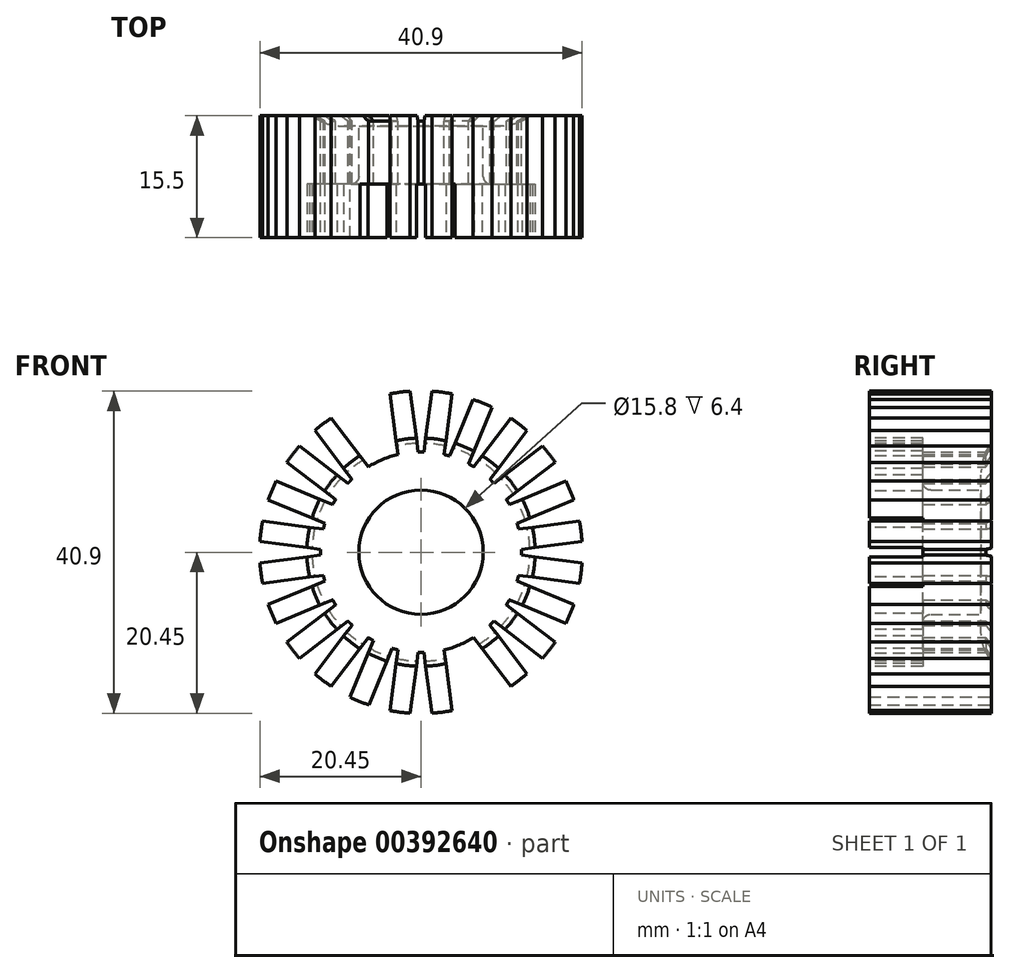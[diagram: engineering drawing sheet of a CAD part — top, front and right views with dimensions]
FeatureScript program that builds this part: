
annotation { "Feature Type Name" : "Feature", "Feature Type Description" : "" }
export const myFeature = defineFeature(function(context is Context, id is Id, definition is map)
    precondition{}
    {
        {
            var Q0;
            Q0=qCreatedBy(makeId("Front.planeOp"),FACE);
            var sketch = newSketch(context, id + "F0", { "sketchPlane" : qUnion([Q0])});
            skCircle(sketch, "E0", {"center": v(0, 0) * mm, "radius": 7.9 * mm});
            skCircle(sketch, "E1", {"center": v(0, 0) * mm, "radius": 12.75 * mm});
            skLineSegment(sketch, "E2", {"start": v(-29.1, 0) * mm, "end": v(30.08, 0) * mm, "construction": true});
            skLineSegment(sketch, "E3", {"start": v(4.61, 35.03) * mm, "end": v(-4.61, -35.03) * mm, "construction": true});
            skLineSegment(sketch, "E4", {"start": v(0.37, 12.74) * mm, "end": v(1.38, 20.45) * mm});
            skLineSegment(sketch, "E5", {"start": v(2.94, 12.4) * mm, "end": v(3.96, 20.11) * mm});
            skArc(sketch, "E6.trimOffspring", {"start": v(3.96, 20.11) * mm, "mid": v(2.68, 20.32) * mm, "end": v(1.38, 20.45) * mm});
            skLineSegment(sketch, "E7.1.0", {"start": v(6.05, 11.22) * mm, "end": v(9.03, 18.4) * mm});
            skArc(sketch, "E7.1.1", {"start": v(9.03, 18.4) * mm, "mid": v(7.85, 18.94) * mm, "end": v(6.63, 19.4) * mm});
            skLineSegment(sketch, "E7.1.2", {"start": v(3.65, 12.22) * mm, "end": v(6.63, 19.4) * mm});
            skLineSegment(sketch, "E7.2.0", {"start": v(8.75, 9.27) * mm, "end": v(13.49, 15.44) * mm});
            skArc(sketch, "E7.2.1", {"start": v(13.49, 15.44) * mm, "mid": v(12.48, 16.26) * mm, "end": v(11.42, 17.02) * mm});
            skLineSegment(sketch, "E7.2.2", {"start": v(6.69, 10.85) * mm, "end": v(11.42, 17.02) * mm});
            skLineSegment(sketch, "E7.3.0", {"start": v(10.85, 6.69) * mm, "end": v(17.02, 11.42) * mm});
            skArc(sketch, "E7.3.1", {"start": v(17.02, 11.42) * mm, "mid": v(16.26, 12.48) * mm, "end": v(15.44, 13.49) * mm});
            skLineSegment(sketch, "E7.3.2", {"start": v(9.27, 8.75) * mm, "end": v(15.44, 13.49) * mm});
            skLineSegment(sketch, "E7.4.0", {"start": v(12.22, 3.65) * mm, "end": v(19.4, 6.63) * mm});
            skArc(sketch, "E7.4.1", {"start": v(19.4, 6.63) * mm, "mid": v(18.94, 7.85) * mm, "end": v(18.4, 9.03) * mm});
            skLineSegment(sketch, "E7.4.2", {"start": v(11.22, 6.05) * mm, "end": v(18.4, 9.03) * mm});
            skLineSegment(sketch, "E7.5.0", {"start": v(12.74, 0.37) * mm, "end": v(20.45, 1.38) * mm});
            skArc(sketch, "E7.5.1", {"start": v(20.45, 1.38) * mm, "mid": v(20.32, 2.68) * mm, "end": v(20.11, 3.96) * mm});
            skLineSegment(sketch, "E7.5.2", {"start": v(12.4, 2.94) * mm, "end": v(20.11, 3.96) * mm});
            skLineSegment(sketch, "E7.6.0", {"start": v(12.4, -2.94) * mm, "end": v(20.11, -3.96) * mm});
            skArc(sketch, "E7.6.1", {"start": v(20.11, -3.96) * mm, "mid": v(20.32, -2.68) * mm, "end": v(20.45, -1.38) * mm});
            skLineSegment(sketch, "E7.6.2", {"start": v(12.74, -0.37) * mm, "end": v(20.45, -1.38) * mm});
            skLineSegment(sketch, "E7.7.0", {"start": v(11.22, -6.05) * mm, "end": v(18.4, -9.03) * mm});
            skArc(sketch, "E7.7.1", {"start": v(18.4, -9.03) * mm, "mid": v(18.94, -7.85) * mm, "end": v(19.4, -6.63) * mm});
            skLineSegment(sketch, "E7.7.2", {"start": v(12.22, -3.65) * mm, "end": v(19.4, -6.63) * mm});
            skLineSegment(sketch, "E7.anchor1", {"start": v(0, 0) * mm, "end": v(2.94, 12.4) * mm, "construction": true});
            skLineSegment(sketch, "E7.anchor2", {"start": v(0, 0) * mm, "end": v(-0.37, 12.74) * mm, "construction": true});
            skLineSegment(sketch, "E8.1.8.0", {"start": v(9.27, -8.75) * mm, "end": v(15.44, -13.49) * mm});
            skArc(sketch, "E8.3.8.0", {"start": v(15.44, -13.49) * mm, "mid": v(16.26, -12.48) * mm, "end": v(17.02, -11.42) * mm});
            skLineSegment(sketch, "E8.7.8.0", {"start": v(10.85, -6.69) * mm, "end": v(17.02, -11.42) * mm});
            skLineSegment(sketch, "E8.1.9.0", {"start": v(6.69, -10.85) * mm, "end": v(11.42, -17.02) * mm});
            skArc(sketch, "E8.3.9.0", {"start": v(11.42, -17.02) * mm, "mid": v(12.48, -16.26) * mm, "end": v(13.49, -15.44) * mm});
            skLineSegment(sketch, "E8.7.9.0", {"start": v(8.75, -9.27) * mm, "end": v(13.49, -15.44) * mm});
            skLineSegment(sketch, "E8.1.10.0", {"start": v(3.65, -12.22) * mm, "end": v(6.63, -19.4) * mm});
            skArc(sketch, "E8.3.10.0", {"start": v(6.63, -19.4) * mm, "mid": v(7.85, -18.94) * mm, "end": v(9.03, -18.4) * mm});
            skLineSegment(sketch, "E8.7.10.0", {"start": v(6.05, -11.22) * mm, "end": v(9.03, -18.4) * mm});
            skLineSegment(sketch, "E8.1.11.0", {"start": v(0.37, -12.74) * mm, "end": v(1.38, -20.45) * mm});
            skArc(sketch, "E8.3.11.0", {"start": v(1.38, -20.45) * mm, "mid": v(2.68, -20.32) * mm, "end": v(3.96, -20.11) * mm});
            skLineSegment(sketch, "E8.7.11.0", {"start": v(2.94, -12.4) * mm, "end": v(3.96, -20.11) * mm});
            skLineSegment(sketch, "E8.1.12.0", {"start": v(-2.94, -12.4) * mm, "end": v(-3.96, -20.11) * mm});
            skArc(sketch, "E8.3.12.0", {"start": v(-3.96, -20.11) * mm, "mid": v(-2.68, -20.32) * mm, "end": v(-1.38, -20.45) * mm});
            skLineSegment(sketch, "E8.7.12.0", {"start": v(-0.37, -12.74) * mm, "end": v(-1.38, -20.45) * mm});
            skLineSegment(sketch, "E8.1.13.0", {"start": v(-6.05, -11.22) * mm, "end": v(-9.03, -18.4) * mm});
            skArc(sketch, "E8.3.13.0", {"start": v(-9.03, -18.4) * mm, "mid": v(-7.85, -18.94) * mm, "end": v(-6.63, -19.4) * mm});
            skLineSegment(sketch, "E8.7.13.0", {"start": v(-3.65, -12.22) * mm, "end": v(-6.63, -19.4) * mm});
            skLineSegment(sketch, "E8.1.14.0", {"start": v(-8.75, -9.27) * mm, "end": v(-13.49, -15.44) * mm});
            skArc(sketch, "E8.3.14.0", {"start": v(-13.49, -15.44) * mm, "mid": v(-12.48, -16.26) * mm, "end": v(-11.42, -17.02) * mm});
            skLineSegment(sketch, "E8.7.14.0", {"start": v(-6.69, -10.85) * mm, "end": v(-11.42, -17.02) * mm});
            skLineSegment(sketch, "E8.1.15.0", {"start": v(-10.85, -6.69) * mm, "end": v(-17.02, -11.42) * mm});
            skArc(sketch, "E8.3.15.0", {"start": v(-17.02, -11.42) * mm, "mid": v(-16.26, -12.48) * mm, "end": v(-15.44, -13.49) * mm});
            skLineSegment(sketch, "E8.7.15.0", {"start": v(-9.27, -8.75) * mm, "end": v(-15.44, -13.49) * mm});
            skLineSegment(sketch, "E8.1.16.0", {"start": v(-12.22, -3.65) * mm, "end": v(-19.4, -6.63) * mm});
            skArc(sketch, "E8.3.16.0", {"start": v(-19.4, -6.63) * mm, "mid": v(-18.94, -7.85) * mm, "end": v(-18.4, -9.03) * mm});
            skLineSegment(sketch, "E8.7.16.0", {"start": v(-11.22, -6.05) * mm, "end": v(-18.4, -9.03) * mm});
            skLineSegment(sketch, "E8.1.17.0", {"start": v(-12.74, -0.37) * mm, "end": v(-20.45, -1.38) * mm});
            skArc(sketch, "E8.3.17.0", {"start": v(-20.45, -1.38) * mm, "mid": v(-20.32, -2.68) * mm, "end": v(-20.11, -3.96) * mm});
            skLineSegment(sketch, "E8.7.17.0", {"start": v(-12.4, -2.94) * mm, "end": v(-20.11, -3.96) * mm});
            skLineSegment(sketch, "E8.1.18.0", {"start": v(-12.4, 2.94) * mm, "end": v(-20.11, 3.96) * mm});
            skArc(sketch, "E8.3.18.0", {"start": v(-20.11, 3.96) * mm, "mid": v(-20.32, 2.68) * mm, "end": v(-20.45, 1.38) * mm});
            skLineSegment(sketch, "E8.7.18.0", {"start": v(-12.74, 0.37) * mm, "end": v(-20.45, 1.38) * mm});
            skLineSegment(sketch, "E8.1.19.0", {"start": v(-11.22, 6.05) * mm, "end": v(-18.4, 9.03) * mm});
            skArc(sketch, "E8.3.19.0", {"start": v(-18.4, 9.03) * mm, "mid": v(-18.94, 7.85) * mm, "end": v(-19.4, 6.63) * mm});
            skLineSegment(sketch, "E8.7.19.0", {"start": v(-12.22, 3.65) * mm, "end": v(-19.4, 6.63) * mm});
            skLineSegment(sketch, "E8.1.20.0", {"start": v(-9.27, 8.75) * mm, "end": v(-15.44, 13.49) * mm});
            skArc(sketch, "E8.3.20.0", {"start": v(-15.44, 13.49) * mm, "mid": v(-16.26, 12.48) * mm, "end": v(-17.02, 11.42) * mm});
            skLineSegment(sketch, "E8.7.20.0", {"start": v(-10.85, 6.69) * mm, "end": v(-17.02, 11.42) * mm});
            skLineSegment(sketch, "E8.1.21.0", {"start": v(-6.69, 10.85) * mm, "end": v(-11.42, 17.02) * mm});
            skArc(sketch, "E8.3.21.0", {"start": v(-11.42, 17.02) * mm, "mid": v(-12.48, 16.26) * mm, "end": v(-13.49, 15.44) * mm});
            skLineSegment(sketch, "E8.7.21.0", {"start": v(-8.75, 9.27) * mm, "end": v(-13.49, 15.44) * mm});
            skLineSegment(sketch, "E8.1.22.0", {"start": v(-3.65, 12.22) * mm, "end": v(-6.63, 19.4) * mm});
            skArc(sketch, "E8.3.22.0", {"start": v(-6.63, 19.4) * mm, "mid": v(-7.85, 18.94) * mm, "end": v(-9.03, 18.4) * mm});
            skLineSegment(sketch, "E8.7.22.0", {"start": v(-6.05, 11.22) * mm, "end": v(-9.03, 18.4) * mm});
            skLineSegment(sketch, "E8.1.23.0", {"start": v(-0.37, 12.74) * mm, "end": v(-1.38, 20.45) * mm});
            skArc(sketch, "E8.3.23.0", {"start": v(-1.38, 20.45) * mm, "mid": v(-2.68, 20.32) * mm, "end": v(-3.96, 20.11) * mm});
            skLineSegment(sketch, "E8.7.23.0", {"start": v(-2.94, 12.4) * mm, "end": v(-3.96, 20.11) * mm});
            skPoint(sketch, "E9", {"position": v(-16.26, 12.48) * mm});
            skPoint(sketch, "E10", {"position": v(16.26, -12.48) * mm});
            skSolve(sketch);
        }
        {
            var Q0;
            Q0=qSketchRegion(id+"F0",true);
            extrude(context, id + "F1", {"entities" : qUnion([Q0]), "depth" : 15.5 * mm});
        }
        {
            var Q0;
            Q0=makeQuery(id+"F1.opExtrude","CAP_FACE",FACE,{"disambiguationData":[OSD([sQuery(id+"F0.wireOp",EDGE,"E0"),sQuery(id+"F0.wireOp",EDGE,"E1"),sQuery(id+"F0.wireOp",EDGE,"E4"),sQuery(id+"F0.wireOp",EDGE,"E5"),sQuery(id+"F0.wireOp",EDGE,"E6.trimOffspring"),sQuery(id+"F0.wireOp",EDGE,"E7.1.0"),sQuery(id+"F0.wireOp",EDGE,"E7.1.1"),sQuery(id+"F0.wireOp",EDGE,"E7.1.2"),sQuery(id+"F0.wireOp",EDGE,"E7.2.0"),sQuery(id+"F0.wireOp",EDGE,"E7.2.1"),sQuery(id+"F0.wireOp",EDGE,"E7.2.2"),sQuery(id+"F0.wireOp",EDGE,"E7.3.0"),sQuery(id+"F0.wireOp",EDGE,"E7.3.1"),sQuery(id+"F0.wireOp",EDGE,"E7.3.2"),sQuery(id+"F0.wireOp",EDGE,"E7.4.0"),sQuery(id+"F0.wireOp",EDGE,"E7.4.1"),sQuery(id+"F0.wireOp",EDGE,"E7.4.2"),sQuery(id+"F0.wireOp",EDGE,"E7.5.0"),sQuery(id+"F0.wireOp",EDGE,"E7.5.1"),sQuery(id+"F0.wireOp",EDGE,"E7.5.2"),sQuery(id+"F0.wireOp",EDGE,"E7.6.0"),sQuery(id+"F0.wireOp",EDGE,"E7.6.1"),sQuery(id+"F0.wireOp",EDGE,"E7.6.2"),sQuery(id+"F0.wireOp",EDGE,"E7.7.0"),sQuery(id+"F0.wireOp",EDGE,"E7.7.1"),sQuery(id+"F0.wireOp",EDGE,"E7.7.2")])],"isStart":false});
            var sketch = newSketch(context, id + "F2", { "sketchPlane" : qUnion([Q0])});
            skCircle(sketch, "E11", {"center": v(0, 0) * mm, "radius": 12.75 * mm});
            skSolve(sketch);
        }
        {
            var Q0;
            Q0=qSketchRegion(id+"F2",true);
            extrude(context, id + "F3", {"entities" : qUnion([Q0]), "operationType" : NewBodyOperationType.REMOVE, "oppositeDirection" : true, "depth" : 6.8 * mm});
        }
        {
            var Q0;
            Q0=makeQuery(id+"F3.boolean.opBoolean","INTERSECT",EDGE,{"derivedFrom":[makeQuery(id+"F1.opExtrude","SWEPT_FACE",FACE,{"disambiguationData":[OSD([sQuery(id+"F0.wireOp",EDGE,"E0")])]}),makeQuery(id+"F3.opExtrude","CAP_FACE",FACE,{"disambiguationData":[OSD([sQuery(id+"F2.wireOp",EDGE,"E11")])],"isStart":false})]});
            fillet(context, id + "F4", {"entities" : qUnion([Q0]), "radius" : 1 * mm, "tangentPropagation" : true, "allowEdgeOverflow" : false});
        }
        {
            var Q0;
            Q0=qCreatedBy(makeId("Right.planeOp"),FACE);
            var sketch = newSketch(context, id + "F5", { "sketchPlane" : qUnion([Q0])});
            skLineSegment(sketch, "E12", {"start": v(0, 0) * mm, "end": v(0, -13.84) * mm});
            skLineSegment(sketch, "E13", {"start": v(-1.3, -10.1) * mm, "end": v(-1.3, 0) * mm});
            skLineSegment(sketch, "E14", {"start": v(0, 0) * mm, "end": v(-1.3, 0) * mm});
            skPoint(sketch, "E15.end.orphan", {"position": v(0, 13.84) * mm});
            skPoint(sketch, "E15.start.orphan", {"position": v(-1.3, 13.84) * mm});
            skArc(sketch, "E16", {"start": v(-1.3, -10.1) * mm, "mid": v(-0.97, -12.08) * mm, "end": v(0, -13.84) * mm});
            skPoint(sketch, "E17.end.orphan", {"position": v(-1.3, -13.84) * mm});
            skSolve(sketch);
        }
        {
            var Q0;
            Q0=qSketchRegion(id+"F5",true);
            var Q1;
            Q1=sQuery(id+"F5.wireOp",EDGE,"E14");
            revolve(context, id + "F6", {"operationType" : NewBodyOperationType.REMOVE, "entities" : qUnion([Q0]), "axis" : qUnion([Q1]), "revolveType" : RevolveType.FULL, "oppositeDirection" : true});
        }
        {
            var Q0;
            {var subQ0=sQuery(id+"F0.wireOp",EDGE,"E8.1.19.0");var subQ1=sQuery(id+"F0.wireOp",EDGE,"E8.3.19.0");var subQ2=sQuery(id+"F0.wireOp",EDGE,"E8.7.19.0");Q0=makeQuery(id+"F3.boolean.opBoolean","SPLIT",FACE,{"disambiguationData":[TD([makeQuery(id+"F1.opExtrude","SWEPT_FACE",FACE,{"disambiguationData":[OSD([subQ0])]})])],"derivedFrom":makeQuery(id+"F1.opExtrude","CAP_FACE",FACE,{"disambiguationData":[OSD([sQuery(id+"F0.wireOp",EDGE,"E0"),sQuery(id+"F0.wireOp",EDGE,"E1"),sQuery(id+"F0.wireOp",EDGE,"E4"),sQuery(id+"F0.wireOp",EDGE,"E5"),sQuery(id+"F0.wireOp",EDGE,"E6.trimOffspring"),sQuery(id+"F0.wireOp",EDGE,"E7.1.0"),sQuery(id+"F0.wireOp",EDGE,"E7.1.1"),sQuery(id+"F0.wireOp",EDGE,"E7.1.2"),sQuery(id+"F0.wireOp",EDGE,"E7.2.0"),sQuery(id+"F0.wireOp",EDGE,"E7.2.1"),sQuery(id+"F0.wireOp",EDGE,"E7.2.2"),sQuery(id+"F0.wireOp",EDGE,"E7.3.0"),sQuery(id+"F0.wireOp",EDGE,"E7.3.1"),sQuery(id+"F0.wireOp",EDGE,"E7.3.2"),sQuery(id+"F0.wireOp",EDGE,"E7.4.0"),sQuery(id+"F0.wireOp",EDGE,"E7.4.1"),sQuery(id+"F0.wireOp",EDGE,"E7.4.2"),sQuery(id+"F0.wireOp",EDGE,"E7.5.0"),sQuery(id+"F0.wireOp",EDGE,"E7.5.1"),sQuery(id+"F0.wireOp",EDGE,"E7.5.2"),sQuery(id+"F0.wireOp",EDGE,"E7.6.0"),sQuery(id+"F0.wireOp",EDGE,"E7.6.1"),sQuery(id+"F0.wireOp",EDGE,"E7.6.2"),sQuery(id+"F0.wireOp",EDGE,"E7.7.0"),sQuery(id+"F0.wireOp",EDGE,"E7.7.1"),sQuery(id+"F0.wireOp",EDGE,"E7.7.2"),sQuery(id+"F0.wireOp",EDGE,"E8.1.8.0"),sQuery(id+"F0.wireOp",EDGE,"E8.3.8.0"),sQuery(id+"F0.wireOp",EDGE,"E8.7.8.0"),sQuery(id+"F0.wireOp",EDGE,"E8.1.9.0"),sQuery(id+"F0.wireOp",EDGE,"E8.3.9.0"),sQuery(id+"F0.wireOp",EDGE,"E8.7.9.0"),sQuery(id+"F0.wireOp",EDGE,"E8.1.10.0"),sQuery(id+"F0.wireOp",EDGE,"E8.3.10.0"),sQuery(id+"F0.wireOp",EDGE,"E8.7.10.0"),sQuery(id+"F0.wireOp",EDGE,"E8.1.11.0"),sQuery(id+"F0.wireOp",EDGE,"E8.3.11.0"),sQuery(id+"F0.wireOp",EDGE,"E8.7.11.0"),sQuery(id+"F0.wireOp",EDGE,"E8.1.12.0"),sQuery(id+"F0.wireOp",EDGE,"E8.3.12.0"),sQuery(id+"F0.wireOp",EDGE,"E8.7.12.0"),sQuery(id+"F0.wireOp",EDGE,"E8.1.13.0"),sQuery(id+"F0.wireOp",EDGE,"E8.3.13.0"),sQuery(id+"F0.wireOp",EDGE,"E8.7.13.0"),sQuery(id+"F0.wireOp",EDGE,"E8.1.14.0"),sQuery(id+"F0.wireOp",EDGE,"E8.3.14.0"),sQuery(id+"F0.wireOp",EDGE,"E8.7.14.0"),sQuery(id+"F0.wireOp",EDGE,"E8.1.15.0"),sQuery(id+"F0.wireOp",EDGE,"E8.3.15.0"),sQuery(id+"F0.wireOp",EDGE,"E8.7.15.0"),sQuery(id+"F0.wireOp",EDGE,"E8.1.16.0"),sQuery(id+"F0.wireOp",EDGE,"E8.3.16.0"),sQuery(id+"F0.wireOp",EDGE,"E8.7.16.0"),sQuery(id+"F0.wireOp",EDGE,"E8.1.17.0"),sQuery(id+"F0.wireOp",EDGE,"E8.3.17.0"),sQuery(id+"F0.wireOp",EDGE,"E8.7.17.0"),sQuery(id+"F0.wireOp",EDGE,"E8.1.18.0"),sQuery(id+"F0.wireOp",EDGE,"E8.3.18.0"),sQuery(id+"F0.wireOp",EDGE,"E8.7.18.0"),subQ0,subQ1,subQ2,sQuery(id+"F0.wireOp",EDGE,"E8.1.20.0"),sQuery(id+"F0.wireOp",EDGE,"E8.3.20.0"),sQuery(id+"F0.wireOp",EDGE,"E8.7.20.0"),sQuery(id+"F0.wireOp",EDGE,"E8.1.21.0"),sQuery(id+"F0.wireOp",EDGE,"E8.3.21.0"),sQuery(id+"F0.wireOp",EDGE,"E8.7.21.0"),sQuery(id+"F0.wireOp",EDGE,"E8.1.22.0"),sQuery(id+"F0.wireOp",EDGE,"E8.3.22.0"),sQuery(id+"F0.wireOp",EDGE,"E8.7.22.0"),sQuery(id+"F0.wireOp",EDGE,"E8.1.23.0"),sQuery(id+"F0.wireOp",EDGE,"E8.3.23.0"),sQuery(id+"F0.wireOp",EDGE,"E8.7.23.0")])],"isStart":false})});}
            var sketch = newSketch(context, id + "F7", { "sketchPlane" : qUnion([Q0])});
            skLineSegment(sketch, "E18", {"start": v(0, 0) * mm, "end": v(-36.63, 0) * mm, "construction": true});
            skLineSegment(sketch, "E19", {"start": v(0, 0) * mm, "end": v(0, 29.2) * mm, "construction": true});
            skCircle(sketch, "E20", {"center": v(0, 0) * mm, "radius": 14.5 * mm});
            skSolve(sketch);
        }
        {
            var Q0;
            Q0=qSketchRegion(id+"F7",true);
            var Q1;
            Q1=makeQuery(id+"F3.boolean.opBoolean","COPY",FACE,{"derivedFrom":makeQuery(id+"F3.opExtrude","CAP_FACE",FACE,{"disambiguationData":[OSD([sQuery(id+"F2.wireOp",EDGE,"E11")])],"isStart":false})});
            extrude(context, id + "F8", {"entities" : qUnion([Q0]), "operationType" : NewBodyOperationType.REMOVE, "endBound" : BoundingType.UP_TO_SURFACE, "oppositeDirection" : true, "endBoundEntityFace" : qUnion([Q1]), "depth" : 25 * mm});
        }
        {
            var Q0;
            {var subQ0=sQuery(id+"F0.wireOp",EDGE,"E8.1.22.0");var subQ1=sQuery(id+"F0.wireOp",EDGE,"E8.3.22.0");var subQ2=sQuery(id+"F0.wireOp",EDGE,"E8.7.22.0");Q0=makeQuery(id+"F3.boolean.opBoolean","SPLIT",FACE,{"disambiguationData":[TD([makeQuery(id+"F1.opExtrude","SWEPT_FACE",FACE,{"disambiguationData":[OSD([subQ0])]})])],"derivedFrom":makeQuery(id+"F1.opExtrude","CAP_FACE",FACE,{"disambiguationData":[OSD([sQuery(id+"F0.wireOp",EDGE,"E0"),sQuery(id+"F0.wireOp",EDGE,"E1"),sQuery(id+"F0.wireOp",EDGE,"E4"),sQuery(id+"F0.wireOp",EDGE,"E5"),sQuery(id+"F0.wireOp",EDGE,"E6.trimOffspring"),sQuery(id+"F0.wireOp",EDGE,"E7.1.0"),sQuery(id+"F0.wireOp",EDGE,"E7.1.1"),sQuery(id+"F0.wireOp",EDGE,"E7.1.2"),sQuery(id+"F0.wireOp",EDGE,"E7.2.0"),sQuery(id+"F0.wireOp",EDGE,"E7.2.1"),sQuery(id+"F0.wireOp",EDGE,"E7.2.2"),sQuery(id+"F0.wireOp",EDGE,"E7.3.0"),sQuery(id+"F0.wireOp",EDGE,"E7.3.1"),sQuery(id+"F0.wireOp",EDGE,"E7.3.2"),sQuery(id+"F0.wireOp",EDGE,"E7.4.0"),sQuery(id+"F0.wireOp",EDGE,"E7.4.1"),sQuery(id+"F0.wireOp",EDGE,"E7.4.2"),sQuery(id+"F0.wireOp",EDGE,"E7.5.0"),sQuery(id+"F0.wireOp",EDGE,"E7.5.1"),sQuery(id+"F0.wireOp",EDGE,"E7.5.2"),sQuery(id+"F0.wireOp",EDGE,"E7.6.0"),sQuery(id+"F0.wireOp",EDGE,"E7.6.1"),sQuery(id+"F0.wireOp",EDGE,"E7.6.2"),sQuery(id+"F0.wireOp",EDGE,"E7.7.0"),sQuery(id+"F0.wireOp",EDGE,"E7.7.1"),sQuery(id+"F0.wireOp",EDGE,"E7.7.2"),sQuery(id+"F0.wireOp",EDGE,"E8.1.8.0"),sQuery(id+"F0.wireOp",EDGE,"E8.3.8.0"),sQuery(id+"F0.wireOp",EDGE,"E8.7.8.0"),sQuery(id+"F0.wireOp",EDGE,"E8.1.9.0"),sQuery(id+"F0.wireOp",EDGE,"E8.3.9.0"),sQuery(id+"F0.wireOp",EDGE,"E8.7.9.0"),sQuery(id+"F0.wireOp",EDGE,"E8.1.10.0"),sQuery(id+"F0.wireOp",EDGE,"E8.3.10.0"),sQuery(id+"F0.wireOp",EDGE,"E8.7.10.0"),sQuery(id+"F0.wireOp",EDGE,"E8.1.11.0"),sQuery(id+"F0.wireOp",EDGE,"E8.3.11.0"),sQuery(id+"F0.wireOp",EDGE,"E8.7.11.0"),sQuery(id+"F0.wireOp",EDGE,"E8.1.12.0"),sQuery(id+"F0.wireOp",EDGE,"E8.3.12.0"),sQuery(id+"F0.wireOp",EDGE,"E8.7.12.0"),sQuery(id+"F0.wireOp",EDGE,"E8.1.13.0"),sQuery(id+"F0.wireOp",EDGE,"E8.3.13.0"),sQuery(id+"F0.wireOp",EDGE,"E8.7.13.0"),sQuery(id+"F0.wireOp",EDGE,"E8.1.14.0"),sQuery(id+"F0.wireOp",EDGE,"E8.3.14.0"),sQuery(id+"F0.wireOp",EDGE,"E8.7.14.0"),sQuery(id+"F0.wireOp",EDGE,"E8.1.15.0"),sQuery(id+"F0.wireOp",EDGE,"E8.3.15.0"),sQuery(id+"F0.wireOp",EDGE,"E8.7.15.0"),sQuery(id+"F0.wireOp",EDGE,"E8.1.16.0"),sQuery(id+"F0.wireOp",EDGE,"E8.3.16.0"),sQuery(id+"F0.wireOp",EDGE,"E8.7.16.0"),sQuery(id+"F0.wireOp",EDGE,"E8.1.17.0"),sQuery(id+"F0.wireOp",EDGE,"E8.3.17.0"),sQuery(id+"F0.wireOp",EDGE,"E8.7.17.0"),sQuery(id+"F0.wireOp",EDGE,"E8.1.18.0"),sQuery(id+"F0.wireOp",EDGE,"E8.3.18.0"),sQuery(id+"F0.wireOp",EDGE,"E8.7.18.0"),sQuery(id+"F0.wireOp",EDGE,"E8.1.19.0"),sQuery(id+"F0.wireOp",EDGE,"E8.3.19.0"),sQuery(id+"F0.wireOp",EDGE,"E8.7.19.0"),sQuery(id+"F0.wireOp",EDGE,"E8.1.20.0"),sQuery(id+"F0.wireOp",EDGE,"E8.3.20.0"),sQuery(id+"F0.wireOp",EDGE,"E8.7.20.0"),sQuery(id+"F0.wireOp",EDGE,"E8.1.21.0"),sQuery(id+"F0.wireOp",EDGE,"E8.3.21.0"),sQuery(id+"F0.wireOp",EDGE,"E8.7.21.0"),subQ0,subQ1,subQ2,sQuery(id+"F0.wireOp",EDGE,"E8.1.23.0"),sQuery(id+"F0.wireOp",EDGE,"E8.3.23.0"),sQuery(id+"F0.wireOp",EDGE,"E8.7.23.0")])],"isStart":false})});}
            var sketch = newSketch(context, id + "F9", { "sketchPlane" : qUnion([Q0])});
            skLineSegment(sketch, "E21.0", {"start": v(-4.33, 13.84) * mm, "end": v(-6.63, 19.4) * mm});
            skLineSegment(sketch, "E21.1", {"start": v(-6.73, 12.84) * mm, "end": v(-9.03, 18.4) * mm});
            skPoint(sketch, "E21.2", {"position": v(-7.85, 18.94) * mm});
            skLineSegment(sketch, "E22", {"start": v(-6.73, 12.84) * mm, "end": v(-6.05, 11.22) * mm});
            skLineSegment(sketch, "E23", {"start": v(-4.33, 13.84) * mm, "end": v(-3.65, 12.22) * mm});
            skArc(sketch, "E24.0", {"start": v(-6.63, 19.4) * mm, "mid": v(-7.85, 18.94) * mm, "end": v(-9.03, 18.4) * mm});
            skLineSegment(sketch, "E25.0", {"start": v(4.33, -13.84) * mm, "end": v(6.63, -19.4) * mm});
            skArc(sketch, "E25.1", {"start": v(6.63, -19.4) * mm, "mid": v(7.85, -18.94) * mm, "end": v(9.03, -18.4) * mm});
            skLineSegment(sketch, "E25.2", {"start": v(6.73, -12.84) * mm, "end": v(9.03, -18.4) * mm});
            skLineSegment(sketch, "E25.3", {"start": v(3.65, -12.22) * mm, "end": v(4.33, -13.84) * mm});
            skLineSegment(sketch, "E25.4", {"start": v(6.05, -11.22) * mm, "end": v(6.73, -12.84) * mm});
            skArc(sketch, "E26", {"start": v(3.65, -12.22) * mm, "mid": v(4.88, -11.78) * mm, "end": v(6.05, -11.22) * mm});
            skArc(sketch, "E27.trimOffspring", {"start": v(-3.65, 12.22) * mm, "mid": v(-4.88, 11.78) * mm, "end": v(-6.05, 11.22) * mm});
            skSolve(sketch);
        }
        {
            var Q0;
            Q0=qSketchRegion(id+"F9",true);
            extrude(context, id + "F10", {"entities" : qUnion([Q0]), "operationType" : NewBodyOperationType.REMOVE, "oppositeDirection" : true, "depth" : 25 * mm});
        }
    });
